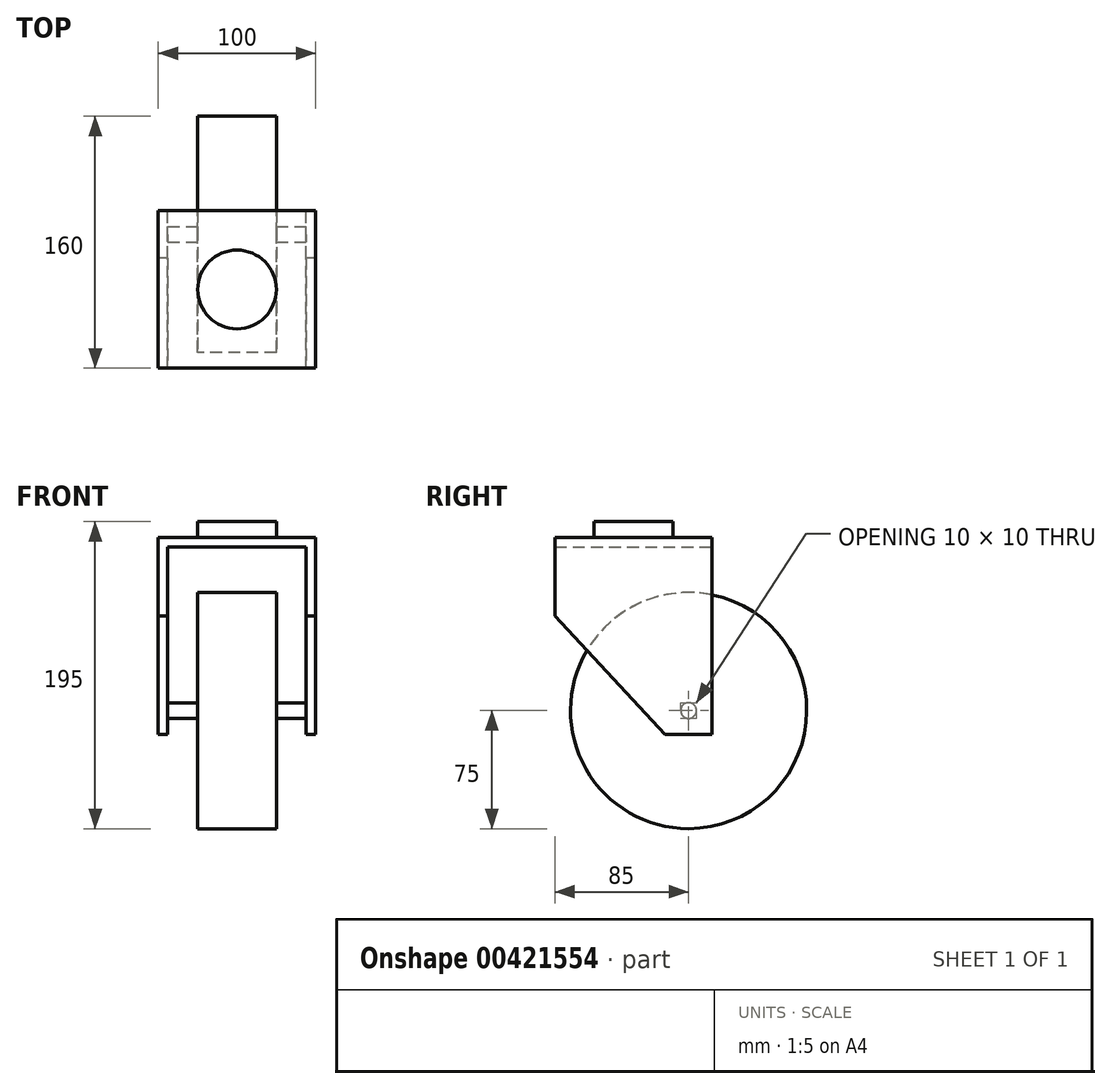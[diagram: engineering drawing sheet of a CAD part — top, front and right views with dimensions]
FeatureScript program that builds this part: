
annotation { "Feature Type Name" : "Feature", "Feature Type Description" : "" }
export const myFeature = defineFeature(function(context is Context, id is Id, definition is map)
    precondition{}
    {
        {
            var Q0;
            Q0=qCreatedBy(makeId("Right.planeOp"),FACE);
            var sketch = newSketch(context, id + "F0", { "sketchPlane" : qUnion([Q0])});
            skLineSegment(sketch, "E0.bottom", {"start": v(0, 0) * mm, "end": v(-100, 0) * mm});
            skLineSegment(sketch, "E0.top", {"start": v(0, -125) * mm, "end": v(-30, -125) * mm});
            skLineSegment(sketch, "E0.left", {"start": v(0, 0) * mm, "end": v(0, -125) * mm});
            skLineSegment(sketch, "E0.right", {"start": v(-100, 0) * mm, "end": v(-100, -50) * mm});
            skLineSegment(sketch, "E1", {"start": v(-100, -50) * mm, "end": v(-30, -125) * mm});
            skSolve(sketch);
        }
        {
            var Q0;
            Q0 = qSketchRegion(id + "F0", true);
            extrude(context, id + "F1", {"entities" : qUnion([Q0]), "endBound" : BoundingType.SYMMETRIC, "depth" : 100 * mm});
        }
        {
            var Q0;
            Q0=makeQuery(id+"F1.opExtrude","SWEPT_FACE",FACE,{"disambiguationData":[OSD([sQuery(id+"F0.wireOp",EDGE,"E0.left")])]});
            var sketch = newSketch(context, id + "F2", { "sketchPlane" : qUnion([Q0])});
            skLineSegment(sketch, "E2.bottom", {"start": v(-44, -125) * mm, "end": v(44, -125) * mm});
            skLineSegment(sketch, "E2.top", {"start": v(-44, -6) * mm, "end": v(44, -6) * mm});
            skLineSegment(sketch, "E2.left", {"start": v(-44, -125) * mm, "end": v(-44, -6) * mm});
            skLineSegment(sketch, "E2.right", {"start": v(44, -125) * mm, "end": v(44, -6) * mm});
            skSolve(sketch);
        }
        {
            var Q0;
            Q0 = qSketchRegion(id + "F2", true);
            extrude(context, id + "F3", {"entities" : qUnion([Q0]), "operationType" : NewBodyOperationType.REMOVE, "endBound" : BoundingType.THROUGH_ALL, "oppositeDirection" : true, "depth" : 25 * mm});
        }
        {
            var Q0;
            Q0=makeQuery(id+"F3.boolean.opBoolean","COPY",FACE,{"derivedFrom":makeQuery(id+"F3.opExtrude","SWEPT_FACE",FACE,{"disambiguationData":[OSD([sQuery(id+"F2.wireOp",EDGE,"E2.left")])]})});
            var sketch = newSketch(context, id + "F4", { "sketchPlane" : qUnion([Q0])});
            skLineSegment(sketch, "E3.bottom", {"start": v(0, -125) * mm, "end": v(15, -125) * mm, "construction": true});
            skLineSegment(sketch, "E3.top", {"start": v(0, -110) * mm, "end": v(15, -110) * mm, "construction": true});
            skLineSegment(sketch, "E3.left", {"start": v(0, -125) * mm, "end": v(0, -110) * mm, "construction": true});
            skLineSegment(sketch, "E3.right", {"start": v(15, -125) * mm, "end": v(15, -110) * mm, "construction": true});
            skCircle(sketch, "E4", {"center": v(15, -110) * mm, "radius": 5 * mm});
            skSolve(sketch);
        }
        {
            var Q0;
            Q0 = qSketchRegion(id + "F4", true);
            extrude(context, id + "F5", {"entities" : qUnion([Q0]), "operationType" : NewBodyOperationType.ADD, "endBound" : BoundingType.UP_TO_NEXT, "depth" : 25 * mm});
        }
        {
            var Q0;
            Q0=makeQuery(id+"F1.opExtrude","SWEPT_FACE",FACE,{"disambiguationData":[OSD([sQuery(id+"F0.wireOp",EDGE,"E0.bottom")])]});
            var sketch = newSketch(context, id + "F6", { "sketchPlane" : qUnion([Q0])});
            skLineSegment(sketch, "E5", {"start": v(-50, -50) * mm, "end": v(0, -50) * mm, "construction": true});
            skLineSegment(sketch, "E6", {"start": v(0, -50) * mm, "end": v(0, 0) * mm, "construction": true});
            skCircle(sketch, "E7", {"center": v(0, -50) * mm, "radius": 25 * mm});
            skSolve(sketch);
        }
        {
            var Q0;
            Q0 = qSketchRegion(id + "F6", true);
            extrude(context, id + "F7", {"entities" : qUnion([Q0]), "operationType" : NewBodyOperationType.ADD, "depth" : 10 * mm});
        }
        {
            var Q0;
            Q0=qCreatedBy(makeId("Right.planeOp"),FACE);
            var sketch = newSketch(context, id + "F8", { "sketchPlane" : qUnion([Q0])});
            skCircle(sketch, "E8", {"center": v(-15, -110) * mm, "radius": 75 * mm});
            skSolve(sketch);
        }
        {
            var Q0;
            Q0 = qSketchRegion(id + "F8", true);
            extrude(context, id + "F9", {"entities" : qUnion([Q0]), "operationType" : NewBodyOperationType.ADD, "endBound" : BoundingType.SYMMETRIC, "depth" : 50 * mm});
        }
    });
